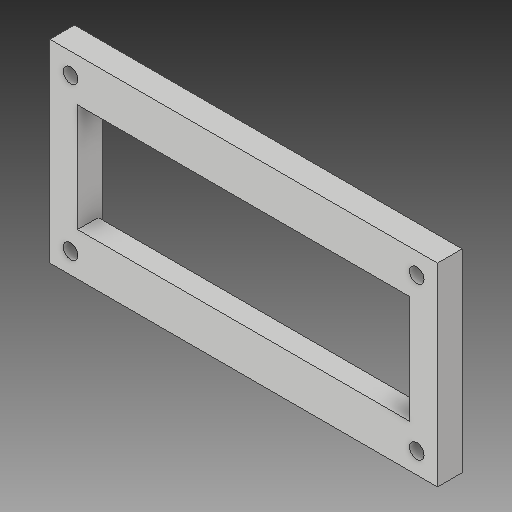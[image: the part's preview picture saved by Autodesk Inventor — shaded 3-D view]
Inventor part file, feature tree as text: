
AUTODESK INVENTOR PART (.ipt)
format: ipt  version: 2018 (Build 220112000, 112)  size: 132,608 bytes
history: native  units: in
note: dims shown in document units (in); Inventor stores cm internally (conversion verified against a paired STEP export)
features: sketch x3, extrude x2, hole x2, projected_geometry x1
ambient origin geometry x8: Origin, YZ Plane, XZ Plane, XY Plane, X Axis, Y Axis, Z Axis, Center Point
bodies: Body1 (feature_tree)
feature tree (8):
  extrude  "Extrusion6"  Depth=3.5in
  extrude  "Extrusion7"  Depth=6.0in
  hole  "Hole4"  [1 undecoded]
  sketch  "Sketch6"  dims[d36=7.0in d37=3.5in]
  sketch  "Sketch7"  dims[d38=2.2in d39=6.0in]
  projected_geometry  "Projected Loop4"
  sketch  "Sketch9"  dims[d40=0.07in d41=0.0in d42=0.125in d43=0.125in d44=0.375in d45=0.0in d53=0.266in d54=0.75in d55=0.375in d56=0.25in d57=0.5635in d58=1.0in d59=0.0in]
  hole  "Hole3"  [1 undecoded]
note: 2 required parameter values undecoded (feature->parameter linkage not recoverable at this tier; creation-order binding heuristic only, values carry confidence <= 0.55)
